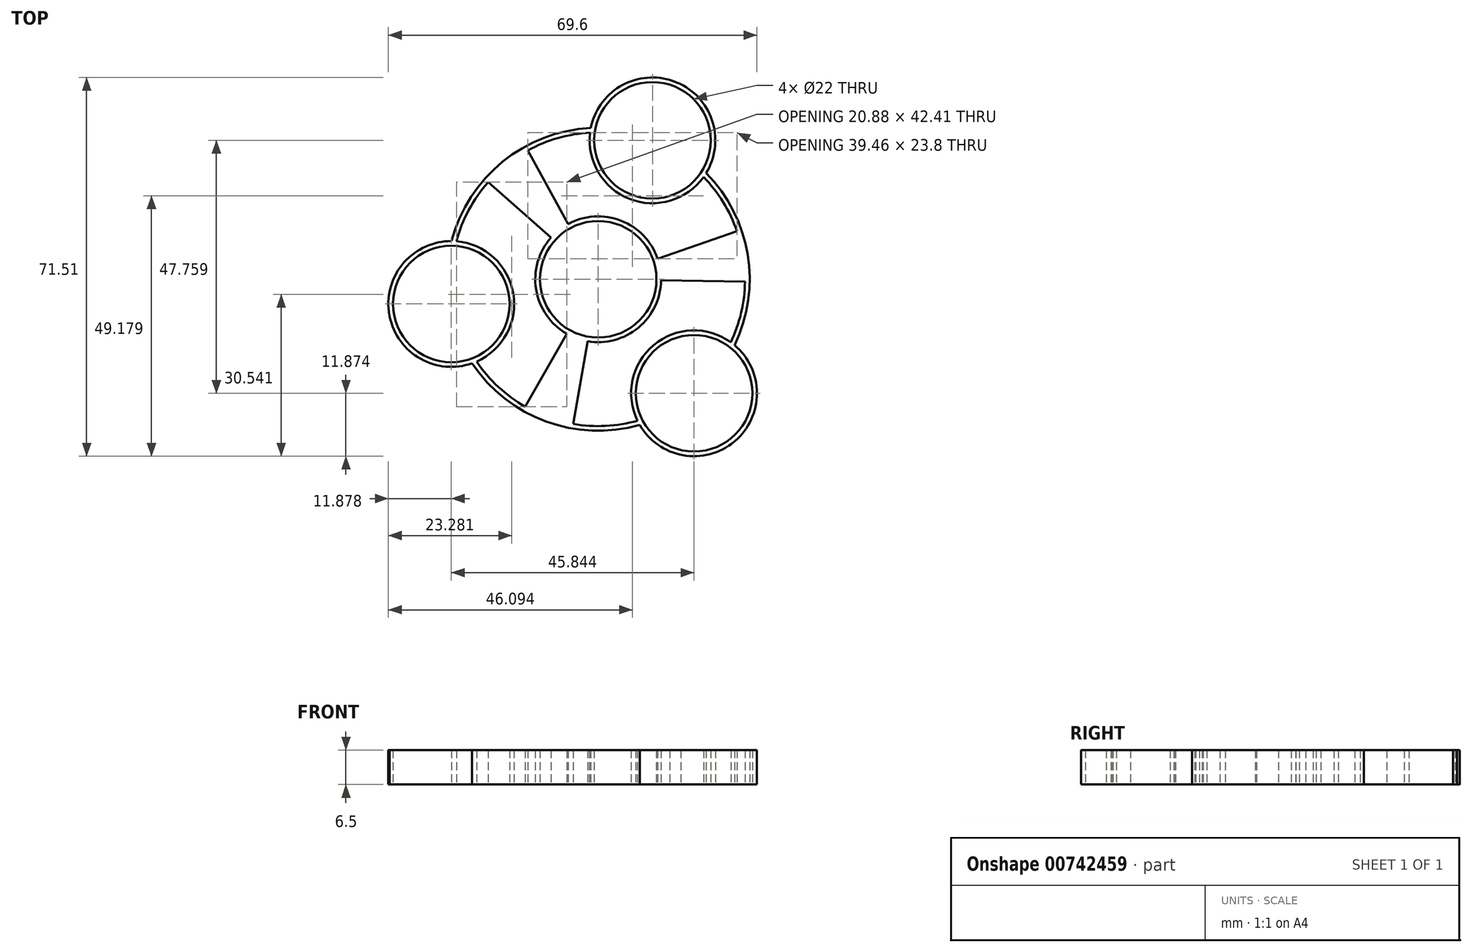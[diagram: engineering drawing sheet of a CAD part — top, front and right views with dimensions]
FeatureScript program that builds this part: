
annotation { "Feature Type Name" : "Feature", "Feature Type Description" : "" }
export const myFeature = defineFeature(function(context is Context, id is Id, definition is map)
    precondition{}
    {
        {
            var Q0;
            Q0=qCreatedBy(makeId("Top.planeOp"),FACE);
            var sketch = newSketch(context, id + "F0", { "sketchPlane" : qUnion([Q0])});
            skCircle(sketch, "E0", {"center": v(0, 0) * mm, "radius": 11 * mm});
            skCircle(sketch, "E1", {"center": v(0, 0) * mm, "radius": 40 * mm});
            skCircle(sketch, "E2", {"center": v(0, 0) * mm, "radius": 39.12 * mm});
            skCircle(sketch, "E3.cCircle", {"center": v(0, 0) * mm, "radius": 39.12 * mm, "construction": true});
            skLineSegment(sketch, "E3.0", {"start": v(16.75, 17.36) * mm, "end": v(21.9, -11.2) * mm});
            skLineSegment(sketch, "E3.1", {"start": v(7.26, -23.4) * mm, "end": v(-20.9, -13.28) * mm});
            skLineSegment(sketch, "E3.2", {"start": v(-23.7, 5.57) * mm, "end": v(-0.7, 25.04) * mm});
            skCircle(sketch, "E4", {"center": v(10.24, 26.23) * mm, "radius": 11 * mm});
            skCircle(sketch, "E5", {"center": v(-27.74, -4.67) * mm, "radius": 11 * mm});
            skCircle(sketch, "E6", {"center": v(18.1, -21.53) * mm, "radius": 11 * mm});
            skPoint(sketch, "E7.orphan", {"position": v(13.24, 36.82) * mm});
            skPoint(sketch, "E8.orphan", {"position": v(25.27, -29.87) * mm});
            skPoint(sketch, "E9.orphan", {"position": v(-38.5, -6.95) * mm});
            skCircle(sketch, "E10", {"center": v(10.24, 26.23) * mm, "radius": 11.88 * mm});
            skCircle(sketch, "E11", {"center": v(-27.74, -4.67) * mm, "radius": 11.88 * mm});
            skCircle(sketch, "E12", {"center": v(18.1, -21.53) * mm, "radius": 11.88 * mm});
            skPoint(sketch, "E13", {"position": v(-12.2, 15.3) * mm});
            skLineSegment(sketch, "E14", {"start": v(0, 0) * mm, "end": v(-12.2, 15.3) * mm});
            skLineSegment(sketch, "E15", {"start": v(-12.2, 15.3) * mm, "end": v(-24.94, 31.28) * mm});
            skPoint(sketch, "E16", {"position": v(19.32, 3.08) * mm});
            skPoint(sketch, "E17", {"position": v(-6.82, -18.34) * mm});
            skLineSegment(sketch, "E18", {"start": v(0, 0) * mm, "end": v(19.32, 3.08) * mm});
            skLineSegment(sketch, "E19", {"start": v(19.32, 3.08) * mm, "end": v(39.5, 6.3) * mm});
            skLineSegment(sketch, "E20", {"start": v(0, 0) * mm, "end": v(-6.82, -18.34) * mm});
            skLineSegment(sketch, "E21", {"start": v(-6.82, -18.34) * mm, "end": v(-13.73, -37.57) * mm});
            skLineSegment(sketch, "E22", {"start": v(0, 0) * mm, "end": v(-19.13, 35.13) * mm});
            skLineSegment(sketch, "E23", {"start": v(0, 0) * mm, "end": v(-29.99, 26.47) * mm});
            skLineSegment(sketch, "E24", {"start": v(0, 0) * mm, "end": v(37.8, 13.06) * mm});
            skLineSegment(sketch, "E25", {"start": v(0, 0) * mm, "end": v(40, -0.66) * mm});
            skLineSegment(sketch, "E26", {"start": v(0, 0) * mm, "end": v(-19.86, -34.72) * mm});
            skLineSegment(sketch, "E27", {"start": v(0, 0) * mm, "end": v(-6.8, -39.42) * mm});
            skCircle(sketch, "E28", {"center": v(0, 0) * mm, "radius": 27.72 * mm});
            skCircle(sketch, "E29", {"center": v(0, 0) * mm, "radius": 28.6 * mm});
            skCircle(sketch, "E30", {"center": v(0, 0) * mm, "radius": 11.88 * mm});
            skSolve(sketch);
        }
        {
            var Q0;
            {var subQ0=sQuery(id+"F0.wireOp",EDGE,"E28");var subQ1=sQuery(id+"F0.wireOp",EDGE,"E11");var subQ2=makeQuery(id+"F0.imprint","INTERSECT",VERTEX,{"disambiguationData":[OD(0.0)],"derivedFrom":[subQ1,subQ0]});Q0=makeQuery(id+"F0.imprint","IMPRINT",FACE,{"disambiguationData":[TD([[makeQuery(id+"F0.imprint","IMPRINT",EDGE,{"disambiguationData":[TD([[subQ2,-1.0]])],"derivedFrom":subQ1}),-1.0]])]});}
            var Q1;
            {var subQ1=sQuery(id+"F0.wireOp",EDGE,"E3.2");var subQ3=sQuery(id+"F0.wireOp",EDGE,"E23");var subQ4=makeQuery(id+"F0.imprint","INTERSECT",VERTEX,{"derivedFrom":[subQ1,subQ3]});Q1=makeQuery(id+"F0.imprint","IMPRINT",FACE,{"disambiguationData":[TD([[makeQuery(id+"F0.imprint","IMPRINT",EDGE,{"disambiguationData":[TD([[subQ4,-1.0]])],"derivedFrom":subQ3}),-1.0]])]});}
            var Q2;
            {var subQ0=sQuery(id+"F0.wireOp",EDGE,"E28");var subQ1=sQuery(id+"F0.wireOp",EDGE,"E15");var subQ2=makeQuery(id+"F0.imprint","INTERSECT",VERTEX,{"derivedFrom":[subQ1,subQ0]});Q2=makeQuery(id+"F0.imprint","IMPRINT",FACE,{"disambiguationData":[TD([[makeQuery(id+"F0.imprint","IMPRINT",EDGE,{"disambiguationData":[TD([[subQ2,-1.0]])],"derivedFrom":subQ1}),-1.0]])]});}
            var Q3;
            {var subQ0=sQuery(id+"F0.wireOp",EDGE,"E28");var subQ1=sQuery(id+"F0.wireOp",EDGE,"E15");var subQ2=makeQuery(id+"F0.imprint","INTERSECT",VERTEX,{"derivedFrom":[subQ1,subQ0]});Q3=makeQuery(id+"F0.imprint","IMPRINT",FACE,{"disambiguationData":[TD([[makeQuery(id+"F0.imprint","IMPRINT",EDGE,{"disambiguationData":[TD([[subQ2,-1.0]])],"derivedFrom":subQ1}),1.0]])]});}
            var Q4;
            {var subQ1=sQuery(id+"F0.wireOp",EDGE,"E3.2");var subQ3=sQuery(id+"F0.wireOp",EDGE,"E22");var subQ4=makeQuery(id+"F0.imprint","INTERSECT",VERTEX,{"derivedFrom":[subQ1,subQ3]});Q4=makeQuery(id+"F0.imprint","IMPRINT",FACE,{"disambiguationData":[TD([[makeQuery(id+"F0.imprint","IMPRINT",EDGE,{"disambiguationData":[TD([[subQ4,-1.0]])],"derivedFrom":subQ3}),1.0]])]});}
            var Q5;
            {var subQ0=sQuery(id+"F0.wireOp",EDGE,"E29");var subQ1=sQuery(id+"F0.wireOp",EDGE,"E10");var subQ2=makeQuery(id+"F0.imprint","INTERSECT",VERTEX,{"disambiguationData":[OD(0.0)],"derivedFrom":[subQ1,subQ0]});Q5=makeQuery(id+"F0.imprint","IMPRINT",FACE,{"disambiguationData":[TD([[makeQuery(id+"F0.imprint","IMPRINT",EDGE,{"disambiguationData":[TD([[subQ2,-1.0]])],"derivedFrom":subQ1}),-1.0]])]});}
            var Q6;
            {var subQ0=sQuery(id+"F0.wireOp",EDGE,"E29");var subQ1=sQuery(id+"F0.wireOp",EDGE,"E4");var subQ2=makeQuery(id+"F0.imprint","INTERSECT",VERTEX,{"disambiguationData":[OD(0.0)],"derivedFrom":[subQ1,subQ0]});Q6=makeQuery(id+"F0.imprint","IMPRINT",FACE,{"disambiguationData":[TD([[makeQuery(id+"F0.imprint","IMPRINT",EDGE,{"disambiguationData":[TD([[subQ2,-1.0]])],"derivedFrom":subQ1}),-1.0]])]});}
            var Q7;
            {var subQ0=sQuery(id+"F0.wireOp",EDGE,"E4");var subQ1=sQuery(id+"F0.wireOp",EDGE,"E3.2");var subQ2=makeQuery(id+"F0.imprint","INTERSECT",VERTEX,{"derivedFrom":[subQ1,subQ0]});Q7=makeQuery(id+"F0.imprint","IMPRINT",FACE,{"disambiguationData":[TD([[makeQuery(id+"F0.imprint","IMPRINT",EDGE,{"disambiguationData":[TD([[subQ2,1.0]])],"derivedFrom":subQ1}),1.0]])]});}
            var Q8;
            {var subQ0=sQuery(id+"F0.wireOp",EDGE,"E4");var subQ1=sQuery(id+"F0.wireOp",EDGE,"E3.0");var subQ2=makeQuery(id+"F0.imprint","INTERSECT",VERTEX,{"derivedFrom":[subQ1,subQ0]});Q8=makeQuery(id+"F0.imprint","IMPRINT",FACE,{"disambiguationData":[TD([[makeQuery(id+"F0.imprint","IMPRINT",EDGE,{"disambiguationData":[TD([[subQ2,-1.0]])],"derivedFrom":subQ1}),-1.0]])]});}
            var Q9;
            {var subQ0=sQuery(id+"F0.wireOp",EDGE,"E4");var subQ1=sQuery(id+"F0.wireOp",EDGE,"E2");var subQ2=makeQuery(id+"F0.imprint","INTERSECT",VERTEX,{"disambiguationData":[OD(1.0)],"derivedFrom":[subQ1,subQ0]});Q9=makeQuery(id+"F0.imprint","IMPRINT",FACE,{"disambiguationData":[TD([[makeQuery(id+"F0.imprint","IMPRINT",EDGE,{"disambiguationData":[TD([[subQ2,-1.0]])],"derivedFrom":subQ1}),1.0]])]});}
            var Q10;
            {var subQ4=sQuery(id+"F0.wireOp",EDGE,"E10");var subQ7=sQuery(id+"F0.wireOp",EDGE,"E1");var subQ8=makeQuery(id+"F0.imprint","INTERSECT",VERTEX,{"disambiguationData":[OD(0.0)],"derivedFrom":[subQ7,subQ4]});Q10=makeQuery(id+"F0.imprint","IMPRINT",FACE,{"disambiguationData":[TD([[makeQuery(id+"F0.imprint","IMPRINT",EDGE,{"disambiguationData":[TD([[subQ8,-1.0]])],"derivedFrom":subQ7}),1.0]])]});}
            var Q11;
            {var subQ0=sQuery(id+"F0.wireOp",EDGE,"E10");var subQ1=sQuery(id+"F0.wireOp",EDGE,"E2");var subQ2=makeQuery(id+"F0.imprint","INTERSECT",VERTEX,{"disambiguationData":[OD(0.0)],"derivedFrom":[subQ1,subQ0]});Q11=makeQuery(id+"F0.imprint","IMPRINT",FACE,{"disambiguationData":[TD([[makeQuery(id+"F0.imprint","IMPRINT",EDGE,{"disambiguationData":[TD([[subQ2,-1.0]])],"derivedFrom":subQ1}),1.0]])]});}
            var Q12;
            {var subQ0=sQuery(id+"F0.wireOp",EDGE,"E28");var subQ1=sQuery(id+"F0.wireOp",EDGE,"E4");var subQ2=makeQuery(id+"F0.imprint","INTERSECT",VERTEX,{"disambiguationData":[OD(1.0)],"derivedFrom":[subQ1,subQ0]});Q12=makeQuery(id+"F0.imprint","IMPRINT",FACE,{"disambiguationData":[TD([[makeQuery(id+"F0.imprint","IMPRINT",EDGE,{"disambiguationData":[TD([[subQ2,-1.0]])],"derivedFrom":subQ1}),-1.0]])]});}
            var Q13;
            {var subQ0=sQuery(id+"F0.wireOp",EDGE,"E4");var subQ1=sQuery(id+"F0.wireOp",EDGE,"E3.0");var subQ2=makeQuery(id+"F0.imprint","INTERSECT",VERTEX,{"derivedFrom":[subQ1,subQ0]});Q13=makeQuery(id+"F0.imprint","IMPRINT",FACE,{"disambiguationData":[TD([[makeQuery(id+"F0.imprint","IMPRINT",EDGE,{"disambiguationData":[TD([[subQ2,-1.0]])],"derivedFrom":subQ1}),1.0]])]});}
            var Q14;
            {var subQ0=sQuery(id+"F0.wireOp",EDGE,"E28");var subQ1=sQuery(id+"F0.wireOp",EDGE,"E10");var subQ2=makeQuery(id+"F0.imprint","INTERSECT",VERTEX,{"disambiguationData":[OD(1.0)],"derivedFrom":[subQ1,subQ0]});Q14=makeQuery(id+"F0.imprint","IMPRINT",FACE,{"disambiguationData":[TD([[makeQuery(id+"F0.imprint","IMPRINT",EDGE,{"disambiguationData":[TD([[subQ2,-1.0]])],"derivedFrom":subQ1}),-1.0]])]});}
            var Q15;
            {var subQ0=sQuery(id+"F0.wireOp",EDGE,"E28");var subQ1=sQuery(id+"F0.wireOp",EDGE,"E19");var subQ2=makeQuery(id+"F0.imprint","INTERSECT",VERTEX,{"derivedFrom":[subQ1,subQ0]});Q15=makeQuery(id+"F0.imprint","IMPRINT",FACE,{"disambiguationData":[TD([[makeQuery(id+"F0.imprint","IMPRINT",EDGE,{"disambiguationData":[TD([[subQ2,-1.0]])],"derivedFrom":subQ1}),1.0]])]});}
            var Q16;
            {var subQ0=sQuery(id+"F0.wireOp",EDGE,"E24");var subQ1=sQuery(id+"F0.wireOp",EDGE,"E0");var subQ2=makeQuery(id+"F0.imprint","INTERSECT",VERTEX,{"derivedFrom":[subQ1,subQ0]});Q16=makeQuery(id+"F0.imprint","IMPRINT",FACE,{"disambiguationData":[TD([[makeQuery(id+"F0.imprint","IMPRINT",EDGE,{"disambiguationData":[TD([[subQ2,1.0]])],"derivedFrom":subQ1}),-1.0]])]});}
            var Q17;
            {var subQ0=sQuery(id+"F0.wireOp",EDGE,"E18");var subQ1=sQuery(id+"F0.wireOp",EDGE,"E0");var subQ2=makeQuery(id+"F0.imprint","INTERSECT",VERTEX,{"derivedFrom":[subQ1,subQ0]});Q17=makeQuery(id+"F0.imprint","IMPRINT",FACE,{"disambiguationData":[TD([[makeQuery(id+"F0.imprint","IMPRINT",EDGE,{"disambiguationData":[TD([[subQ2,1.0]])],"derivedFrom":subQ1}),-1.0]])]});}
            var Q18;
            {var subQ1=sQuery(id+"F0.wireOp",EDGE,"E3.0");var subQ3=sQuery(id+"F0.wireOp",EDGE,"E24");var subQ4=makeQuery(id+"F0.imprint","INTERSECT",VERTEX,{"derivedFrom":[subQ1,subQ3]});Q18=makeQuery(id+"F0.imprint","IMPRINT",FACE,{"disambiguationData":[TD([[makeQuery(id+"F0.imprint","IMPRINT",EDGE,{"disambiguationData":[TD([[subQ4,-1.0]])],"derivedFrom":subQ3}),-1.0]])]});}
            var Q19;
            {var subQ1=sQuery(id+"F0.wireOp",EDGE,"E3.0");var subQ3=sQuery(id+"F0.wireOp",EDGE,"E25");var subQ4=makeQuery(id+"F0.imprint","INTERSECT",VERTEX,{"derivedFrom":[subQ1,subQ3]});Q19=makeQuery(id+"F0.imprint","IMPRINT",FACE,{"disambiguationData":[TD([[makeQuery(id+"F0.imprint","IMPRINT",EDGE,{"disambiguationData":[TD([[subQ4,-1.0]])],"derivedFrom":subQ3}),1.0]])]});}
            var Q20;
            {var subQ0=sQuery(id+"F0.wireOp",EDGE,"E14");var subQ1=sQuery(id+"F0.wireOp",EDGE,"E0");var subQ2=makeQuery(id+"F0.imprint","INTERSECT",VERTEX,{"derivedFrom":[subQ1,subQ0]});Q20=makeQuery(id+"F0.imprint","IMPRINT",FACE,{"disambiguationData":[TD([[makeQuery(id+"F0.imprint","IMPRINT",EDGE,{"disambiguationData":[TD([[subQ2,-1.0]])],"derivedFrom":subQ1}),-1.0]])]});}
            var Q21;
            {var subQ0=sQuery(id+"F0.wireOp",EDGE,"E22");var subQ1=sQuery(id+"F0.wireOp",EDGE,"E0");var subQ2=makeQuery(id+"F0.imprint","INTERSECT",VERTEX,{"derivedFrom":[subQ1,subQ0]});Q21=makeQuery(id+"F0.imprint","IMPRINT",FACE,{"disambiguationData":[TD([[makeQuery(id+"F0.imprint","IMPRINT",EDGE,{"disambiguationData":[TD([[subQ2,-1.0]])],"derivedFrom":subQ1}),-1.0]])]});}
            var Q22;
            {var subQ0=sQuery(id+"F0.wireOp",EDGE,"E28");var subQ1=sQuery(id+"F0.wireOp",EDGE,"E19");var subQ2=makeQuery(id+"F0.imprint","INTERSECT",VERTEX,{"derivedFrom":[subQ1,subQ0]});Q22=makeQuery(id+"F0.imprint","IMPRINT",FACE,{"disambiguationData":[TD([[makeQuery(id+"F0.imprint","IMPRINT",EDGE,{"disambiguationData":[TD([[subQ2,-1.0]])],"derivedFrom":subQ1}),-1.0]])]});}
            var Q23;
            {var subQ0=sQuery(id+"F0.wireOp",EDGE,"E6");var subQ1=sQuery(id+"F0.wireOp",EDGE,"E3.0");var subQ2=makeQuery(id+"F0.imprint","INTERSECT",VERTEX,{"derivedFrom":[subQ1,subQ0]});Q23=makeQuery(id+"F0.imprint","IMPRINT",FACE,{"disambiguationData":[TD([[makeQuery(id+"F0.imprint","IMPRINT",EDGE,{"disambiguationData":[TD([[subQ2,1.0]])],"derivedFrom":subQ1}),-1.0]])]});}
            var Q24;
            {var subQ0=sQuery(id+"F0.wireOp",EDGE,"E6");var subQ1=sQuery(id+"F0.wireOp",EDGE,"E3.0");var subQ2=makeQuery(id+"F0.imprint","INTERSECT",VERTEX,{"derivedFrom":[subQ1,subQ0]});Q24=makeQuery(id+"F0.imprint","IMPRINT",FACE,{"disambiguationData":[TD([[makeQuery(id+"F0.imprint","IMPRINT",EDGE,{"disambiguationData":[TD([[subQ2,1.0]])],"derivedFrom":subQ1}),1.0]])]});}
            var Q25;
            {var subQ0=sQuery(id+"F0.wireOp",EDGE,"E28");var subQ1=sQuery(id+"F0.wireOp",EDGE,"E12");var subQ2=makeQuery(id+"F0.imprint","INTERSECT",VERTEX,{"disambiguationData":[OD(0.0)],"derivedFrom":[subQ1,subQ0]});Q25=makeQuery(id+"F0.imprint","IMPRINT",FACE,{"disambiguationData":[TD([[makeQuery(id+"F0.imprint","IMPRINT",EDGE,{"disambiguationData":[TD([[subQ2,1.0]])],"derivedFrom":subQ1}),-1.0]])]});}
            var Q26;
            {var subQ0=sQuery(id+"F0.wireOp",EDGE,"E28");var subQ1=sQuery(id+"F0.wireOp",EDGE,"E6");var subQ2=makeQuery(id+"F0.imprint","INTERSECT",VERTEX,{"disambiguationData":[OD(0.0)],"derivedFrom":[subQ1,subQ0]});Q26=makeQuery(id+"F0.imprint","IMPRINT",FACE,{"disambiguationData":[TD([[makeQuery(id+"F0.imprint","IMPRINT",EDGE,{"disambiguationData":[TD([[subQ2,1.0]])],"derivedFrom":subQ1}),-1.0]])]});}
            var Q27;
            {var subQ0=sQuery(id+"F0.wireOp",EDGE,"E6");var subQ1=sQuery(id+"F0.wireOp",EDGE,"E2");var subQ2=makeQuery(id+"F0.imprint","INTERSECT",VERTEX,{"disambiguationData":[OD(1.0)],"derivedFrom":[subQ1,subQ0]});Q27=makeQuery(id+"F0.imprint","IMPRINT",FACE,{"disambiguationData":[TD([[makeQuery(id+"F0.imprint","IMPRINT",EDGE,{"disambiguationData":[TD([[subQ2,-1.0]])],"derivedFrom":subQ1}),1.0]])]});}
            var Q28;
            {var subQ3=sQuery(id+"F0.wireOp",EDGE,"E12");var subQ7=sQuery(id+"F0.wireOp",EDGE,"E1");var subQ8=makeQuery(id+"F0.imprint","INTERSECT",VERTEX,{"disambiguationData":[OD(0.0)],"derivedFrom":[subQ7,subQ3]});Q28=makeQuery(id+"F0.imprint","IMPRINT",FACE,{"disambiguationData":[TD([[makeQuery(id+"F0.imprint","IMPRINT",EDGE,{"disambiguationData":[TD([[subQ8,-1.0]])],"derivedFrom":subQ7}),1.0]])]});}
            var Q29;
            {var subQ0=sQuery(id+"F0.wireOp",EDGE,"E12");var subQ1=sQuery(id+"F0.wireOp",EDGE,"E2");var subQ2=makeQuery(id+"F0.imprint","INTERSECT",VERTEX,{"disambiguationData":[OD(0.0)],"derivedFrom":[subQ1,subQ0]});Q29=makeQuery(id+"F0.imprint","IMPRINT",FACE,{"disambiguationData":[TD([[makeQuery(id+"F0.imprint","IMPRINT",EDGE,{"disambiguationData":[TD([[subQ2,-1.0]])],"derivedFrom":subQ1}),1.0]])]});}
            var Q30;
            {var subQ0=sQuery(id+"F0.wireOp",EDGE,"E6");var subQ1=sQuery(id+"F0.wireOp",EDGE,"E3.1");var subQ2=makeQuery(id+"F0.imprint","INTERSECT",VERTEX,{"derivedFrom":[subQ1,subQ0]});Q30=makeQuery(id+"F0.imprint","IMPRINT",FACE,{"disambiguationData":[TD([[makeQuery(id+"F0.imprint","IMPRINT",EDGE,{"disambiguationData":[TD([[subQ2,-1.0]])],"derivedFrom":subQ1}),1.0]])]});}
            var Q31;
            {var subQ0=sQuery(id+"F0.wireOp",EDGE,"E28");var subQ1=sQuery(id+"F0.wireOp",EDGE,"E6");var subQ2=makeQuery(id+"F0.imprint","INTERSECT",VERTEX,{"disambiguationData":[OD(1.0)],"derivedFrom":[subQ1,subQ0]});Q31=makeQuery(id+"F0.imprint","IMPRINT",FACE,{"disambiguationData":[TD([[makeQuery(id+"F0.imprint","IMPRINT",EDGE,{"disambiguationData":[TD([[subQ2,-1.0]])],"derivedFrom":subQ1}),-1.0]])]});}
            var Q32;
            {var subQ0=sQuery(id+"F0.wireOp",EDGE,"E28");var subQ1=sQuery(id+"F0.wireOp",EDGE,"E21");var subQ2=makeQuery(id+"F0.imprint","INTERSECT",VERTEX,{"derivedFrom":[subQ1,subQ0]});Q32=makeQuery(id+"F0.imprint","IMPRINT",FACE,{"disambiguationData":[TD([[makeQuery(id+"F0.imprint","IMPRINT",EDGE,{"disambiguationData":[TD([[subQ2,-1.0]])],"derivedFrom":subQ1}),1.0]])]});}
            var Q33;
            {var subQ0=sQuery(id+"F0.wireOp",EDGE,"E28");var subQ1=sQuery(id+"F0.wireOp",EDGE,"E21");var subQ2=makeQuery(id+"F0.imprint","INTERSECT",VERTEX,{"derivedFrom":[subQ1,subQ0]});Q33=makeQuery(id+"F0.imprint","IMPRINT",FACE,{"disambiguationData":[TD([[makeQuery(id+"F0.imprint","IMPRINT",EDGE,{"disambiguationData":[TD([[subQ2,-1.0]])],"derivedFrom":subQ1}),-1.0]])]});}
            var Q34;
            {var subQ1=sQuery(id+"F0.wireOp",EDGE,"E3.1");var subQ3=sQuery(id+"F0.wireOp",EDGE,"E26");var subQ4=makeQuery(id+"F0.imprint","INTERSECT",VERTEX,{"derivedFrom":[subQ1,subQ3]});Q34=makeQuery(id+"F0.imprint","IMPRINT",FACE,{"disambiguationData":[TD([[makeQuery(id+"F0.imprint","IMPRINT",EDGE,{"disambiguationData":[TD([[subQ4,-1.0]])],"derivedFrom":subQ3}),1.0]])]});}
            var Q35;
            {var subQ1=sQuery(id+"F0.wireOp",EDGE,"E3.1");var subQ3=sQuery(id+"F0.wireOp",EDGE,"E27");var subQ4=makeQuery(id+"F0.imprint","INTERSECT",VERTEX,{"derivedFrom":[subQ1,subQ3]});Q35=makeQuery(id+"F0.imprint","IMPRINT",FACE,{"disambiguationData":[TD([[makeQuery(id+"F0.imprint","IMPRINT",EDGE,{"disambiguationData":[TD([[subQ4,-1.0]])],"derivedFrom":subQ3}),-1.0]])]});}
            var Q36;
            {var subQ0=sQuery(id+"F0.wireOp",EDGE,"E20");var subQ1=sQuery(id+"F0.wireOp",EDGE,"E0");var subQ2=makeQuery(id+"F0.imprint","INTERSECT",VERTEX,{"derivedFrom":[subQ1,subQ0]});Q36=makeQuery(id+"F0.imprint","IMPRINT",FACE,{"disambiguationData":[TD([[makeQuery(id+"F0.imprint","IMPRINT",EDGE,{"disambiguationData":[TD([[subQ2,-1.0]])],"derivedFrom":subQ1}),-1.0]])]});}
            var Q37;
            {var subQ0=sQuery(id+"F0.wireOp",EDGE,"E26");var subQ1=sQuery(id+"F0.wireOp",EDGE,"E0");var subQ2=makeQuery(id+"F0.imprint","INTERSECT",VERTEX,{"derivedFrom":[subQ1,subQ0]});Q37=makeQuery(id+"F0.imprint","IMPRINT",FACE,{"disambiguationData":[TD([[makeQuery(id+"F0.imprint","IMPRINT",EDGE,{"disambiguationData":[TD([[subQ2,-1.0]])],"derivedFrom":subQ1}),-1.0]])]});}
            var Q38;
            {var subQ0=sQuery(id+"F0.wireOp",EDGE,"E28");var subQ1=sQuery(id+"F0.wireOp",EDGE,"E5");var subQ2=makeQuery(id+"F0.imprint","INTERSECT",VERTEX,{"disambiguationData":[OD(0.0)],"derivedFrom":[subQ1,subQ0]});Q38=makeQuery(id+"F0.imprint","IMPRINT",FACE,{"disambiguationData":[TD([[makeQuery(id+"F0.imprint","IMPRINT",EDGE,{"disambiguationData":[TD([[subQ2,-1.0]])],"derivedFrom":subQ1}),-1.0]])]});}
            var Q39;
            {var subQ0=sQuery(id+"F0.wireOp",EDGE,"E11");var subQ1=sQuery(id+"F0.wireOp",EDGE,"E2");var subQ2=makeQuery(id+"F0.imprint","INTERSECT",VERTEX,{"disambiguationData":[OD(0.0)],"derivedFrom":[subQ1,subQ0]});Q39=makeQuery(id+"F0.imprint","IMPRINT",FACE,{"disambiguationData":[TD([[makeQuery(id+"F0.imprint","IMPRINT",EDGE,{"disambiguationData":[TD([[subQ2,-1.0]])],"derivedFrom":subQ1}),1.0]])]});}
            var Q40;
            {var subQ0=sQuery(id+"F0.wireOp",EDGE,"E5");var subQ1=sQuery(id+"F0.wireOp",EDGE,"E3.2");var subQ2=makeQuery(id+"F0.imprint","INTERSECT",VERTEX,{"derivedFrom":[subQ1,subQ0]});Q40=makeQuery(id+"F0.imprint","IMPRINT",FACE,{"disambiguationData":[TD([[makeQuery(id+"F0.imprint","IMPRINT",EDGE,{"disambiguationData":[TD([[subQ2,-1.0]])],"derivedFrom":subQ1}),1.0]])]});}
            var Q41;
            {var subQ0=sQuery(id+"F0.wireOp",EDGE,"E5");var subQ1=sQuery(id+"F0.wireOp",EDGE,"E3.1");var subQ2=makeQuery(id+"F0.imprint","INTERSECT",VERTEX,{"derivedFrom":[subQ1,subQ0]});Q41=makeQuery(id+"F0.imprint","IMPRINT",FACE,{"disambiguationData":[TD([[makeQuery(id+"F0.imprint","IMPRINT",EDGE,{"disambiguationData":[TD([[subQ2,1.0]])],"derivedFrom":subQ1}),-1.0]])]});}
            var Q42;
            {var subQ0=sQuery(id+"F0.wireOp",EDGE,"E5");var subQ1=sQuery(id+"F0.wireOp",EDGE,"E2");var subQ2=makeQuery(id+"F0.imprint","INTERSECT",VERTEX,{"disambiguationData":[OD(1.0)],"derivedFrom":[subQ1,subQ0]});Q42=makeQuery(id+"F0.imprint","IMPRINT",FACE,{"disambiguationData":[TD([[makeQuery(id+"F0.imprint","IMPRINT",EDGE,{"disambiguationData":[TD([[subQ2,-1.0]])],"derivedFrom":subQ1}),1.0]])]});}
            var Q43;
            {var subQ0=sQuery(id+"F0.wireOp",EDGE,"E29");var subQ1=sQuery(id+"F0.wireOp",EDGE,"E5");var subQ2=makeQuery(id+"F0.imprint","INTERSECT",VERTEX,{"disambiguationData":[OD(1.0)],"derivedFrom":[subQ1,subQ0]});Q43=makeQuery(id+"F0.imprint","IMPRINT",FACE,{"disambiguationData":[TD([[makeQuery(id+"F0.imprint","IMPRINT",EDGE,{"disambiguationData":[TD([[subQ2,-1.0]])],"derivedFrom":subQ1}),-1.0]])]});}
            var Q44;
            {var subQ0=sQuery(id+"F0.wireOp",EDGE,"E5");var subQ1=sQuery(id+"F0.wireOp",EDGE,"E3.1");var subQ2=makeQuery(id+"F0.imprint","INTERSECT",VERTEX,{"derivedFrom":[subQ1,subQ0]});Q44=makeQuery(id+"F0.imprint","IMPRINT",FACE,{"disambiguationData":[TD([[makeQuery(id+"F0.imprint","IMPRINT",EDGE,{"disambiguationData":[TD([[subQ2,1.0]])],"derivedFrom":subQ1}),1.0]])]});}
            var Q45;
            {var subQ0=sQuery(id+"F0.wireOp",EDGE,"E29");var subQ1=sQuery(id+"F0.wireOp",EDGE,"E11");var subQ2=makeQuery(id+"F0.imprint","INTERSECT",VERTEX,{"disambiguationData":[OD(1.0)],"derivedFrom":[subQ1,subQ0]});Q45=makeQuery(id+"F0.imprint","IMPRINT",FACE,{"disambiguationData":[TD([[makeQuery(id+"F0.imprint","IMPRINT",EDGE,{"disambiguationData":[TD([[subQ2,-1.0]])],"derivedFrom":subQ1}),-1.0]])]});}
            var Q46;
            {var subQ0=sQuery(id+"F0.wireOp",EDGE,"E28");var subQ1=sQuery(id+"F0.wireOp",EDGE,"E12");var subQ2=makeQuery(id+"F0.imprint","INTERSECT",VERTEX,{"disambiguationData":[OD(1.0)],"derivedFrom":[subQ1,subQ0]});Q46=makeQuery(id+"F0.imprint","IMPRINT",FACE,{"disambiguationData":[TD([[makeQuery(id+"F0.imprint","IMPRINT",EDGE,{"disambiguationData":[TD([[subQ2,-1.0]])],"derivedFrom":subQ1}),-1.0]])]});}
            var Q47;
            {var subQ4=sQuery(id+"F0.wireOp",EDGE,"E11");var subQ7=sQuery(id+"F0.wireOp",EDGE,"E1");var subQ8=makeQuery(id+"F0.imprint","INTERSECT",VERTEX,{"disambiguationData":[OD(0.0)],"derivedFrom":[subQ7,subQ4]});Q47=makeQuery(id+"F0.imprint","IMPRINT",FACE,{"disambiguationData":[TD([[makeQuery(id+"F0.imprint","IMPRINT",EDGE,{"disambiguationData":[TD([[subQ8,-1.0]])],"derivedFrom":subQ7}),1.0]])]});}
            var Q48;
            {var subQ0=sQuery(id+"F0.wireOp",EDGE,"E24");var subQ1=sQuery(id+"F0.wireOp",EDGE,"E0");var subQ2=makeQuery(id+"F0.imprint","INTERSECT",VERTEX,{"derivedFrom":[subQ1,subQ0]});Q48=makeQuery(id+"F0.imprint","IMPRINT",FACE,{"disambiguationData":[TD([[makeQuery(id+"F0.imprint","IMPRINT",EDGE,{"disambiguationData":[TD([[subQ2,-1.0]])],"derivedFrom":subQ1}),-1.0]])]});}
            var Q49;
            {var subQ0=sQuery(id+"F0.wireOp",EDGE,"E23");var subQ1=sQuery(id+"F0.wireOp",EDGE,"E0");var subQ2=makeQuery(id+"F0.imprint","INTERSECT",VERTEX,{"derivedFrom":[subQ1,subQ0]});Q49=makeQuery(id+"F0.imprint","IMPRINT",FACE,{"disambiguationData":[TD([[makeQuery(id+"F0.imprint","IMPRINT",EDGE,{"disambiguationData":[TD([[subQ2,-1.0]])],"derivedFrom":subQ1}),-1.0]])]});}
            var Q50;
            {var subQ0=sQuery(id+"F0.wireOp",EDGE,"E27");var subQ1=sQuery(id+"F0.wireOp",EDGE,"E0");var subQ2=makeQuery(id+"F0.imprint","INTERSECT",VERTEX,{"derivedFrom":[subQ1,subQ0]});Q50=makeQuery(id+"F0.imprint","IMPRINT",FACE,{"disambiguationData":[TD([[makeQuery(id+"F0.imprint","IMPRINT",EDGE,{"disambiguationData":[TD([[subQ2,-1.0]])],"derivedFrom":subQ1}),-1.0]])]});}
            var Q51;
            {var subQ1=sQuery(id+"F0.wireOp",EDGE,"E3.0");var subQ3=sQuery(id+"F0.wireOp",EDGE,"E24");var subQ4=makeQuery(id+"F0.imprint","INTERSECT",VERTEX,{"derivedFrom":[subQ1,subQ3]});Q51=makeQuery(id+"F0.imprint","IMPRINT",FACE,{"disambiguationData":[TD([[makeQuery(id+"F0.imprint","IMPRINT",EDGE,{"disambiguationData":[TD([[subQ4,1.0]])],"derivedFrom":subQ3}),-1.0]])]});}
            var Q52;
            {var subQ1=sQuery(id+"F0.wireOp",EDGE,"E3.0");var subQ3=sQuery(id+"F0.wireOp",EDGE,"E25");var subQ4=makeQuery(id+"F0.imprint","INTERSECT",VERTEX,{"derivedFrom":[subQ1,subQ3]});Q52=makeQuery(id+"F0.imprint","IMPRINT",FACE,{"disambiguationData":[TD([[makeQuery(id+"F0.imprint","IMPRINT",EDGE,{"disambiguationData":[TD([[subQ4,1.0]])],"derivedFrom":subQ3}),1.0]])]});}
            var Q53;
            {var subQ1=sQuery(id+"F0.wireOp",EDGE,"E3.2");var subQ3=sQuery(id+"F0.wireOp",EDGE,"E23");var subQ4=makeQuery(id+"F0.imprint","INTERSECT",VERTEX,{"derivedFrom":[subQ1,subQ3]});Q53=makeQuery(id+"F0.imprint","IMPRINT",FACE,{"disambiguationData":[TD([[makeQuery(id+"F0.imprint","IMPRINT",EDGE,{"disambiguationData":[TD([[subQ4,1.0]])],"derivedFrom":subQ3}),-1.0]])]});}
            var Q54;
            {var subQ1=sQuery(id+"F0.wireOp",EDGE,"E3.2");var subQ3=sQuery(id+"F0.wireOp",EDGE,"E22");var subQ4=makeQuery(id+"F0.imprint","INTERSECT",VERTEX,{"derivedFrom":[subQ1,subQ3]});Q54=makeQuery(id+"F0.imprint","IMPRINT",FACE,{"disambiguationData":[TD([[makeQuery(id+"F0.imprint","IMPRINT",EDGE,{"disambiguationData":[TD([[subQ4,1.0]])],"derivedFrom":subQ3}),1.0]])]});}
            var Q55;
            {var subQ1=sQuery(id+"F0.wireOp",EDGE,"E3.1");var subQ3=sQuery(id+"F0.wireOp",EDGE,"E26");var subQ4=makeQuery(id+"F0.imprint","INTERSECT",VERTEX,{"derivedFrom":[subQ1,subQ3]});Q55=makeQuery(id+"F0.imprint","IMPRINT",FACE,{"disambiguationData":[TD([[makeQuery(id+"F0.imprint","IMPRINT",EDGE,{"disambiguationData":[TD([[subQ4,1.0]])],"derivedFrom":subQ3}),1.0]])]});}
            var Q56;
            {var subQ1=sQuery(id+"F0.wireOp",EDGE,"E3.1");var subQ3=sQuery(id+"F0.wireOp",EDGE,"E27");var subQ4=makeQuery(id+"F0.imprint","INTERSECT",VERTEX,{"derivedFrom":[subQ1,subQ3]});Q56=makeQuery(id+"F0.imprint","IMPRINT",FACE,{"disambiguationData":[TD([[makeQuery(id+"F0.imprint","IMPRINT",EDGE,{"disambiguationData":[TD([[subQ4,1.0]])],"derivedFrom":subQ3}),-1.0]])]});}
            extrude(context, id + "F1", {"entities" : qUnion([Q0, Q1, Q2, Q3, Q4, Q5, Q6, Q7, Q8, Q9, Q10, Q11, Q12, Q13, Q14, Q15, Q16, Q17, Q18, Q19, Q20, Q21, Q22, Q23, Q24, Q25, Q26, Q27, Q28, Q29, Q30, Q31, Q32, Q33, Q34, Q35, Q36, Q37, Q38, Q39, Q40, Q41, Q42, Q43, Q44, Q45, Q46, Q47, Q48, Q49, Q50, Q51, Q52, Q53, Q54, Q55, Q56]), "depth" : 6.5 * mm, "offsetDistance" : 25 * mm});
        }
    });
